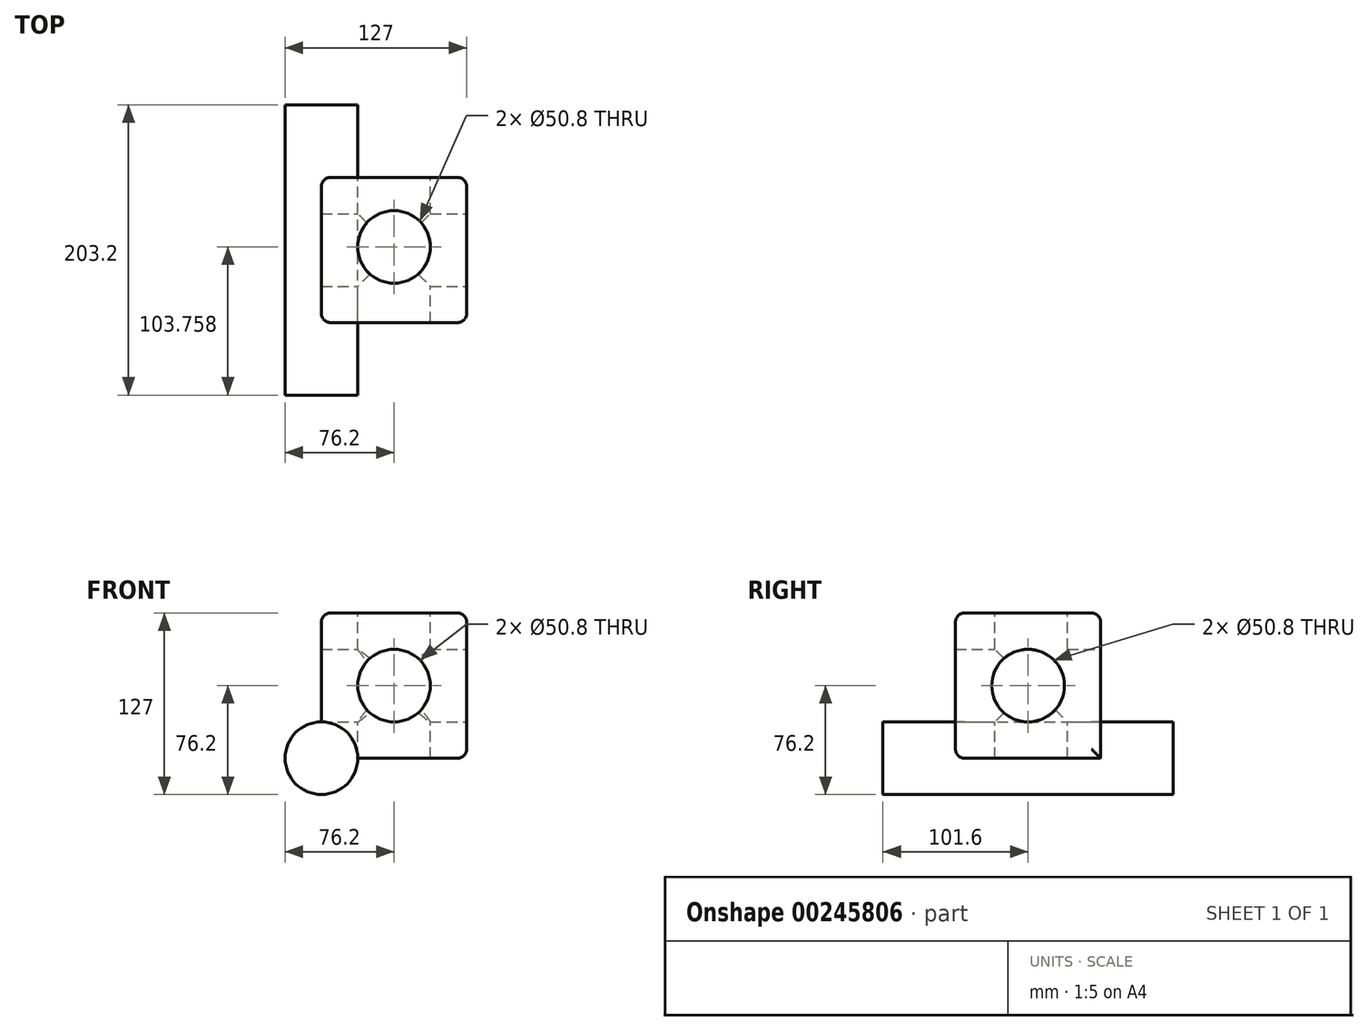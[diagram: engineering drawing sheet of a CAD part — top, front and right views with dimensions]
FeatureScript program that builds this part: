
annotation { "Feature Type Name" : "Feature", "Feature Type Description" : "" }
export const myFeature = defineFeature(function(context is Context, id is Id, definition is map)
    precondition{}
    {
        {
            var Q0;
            Q0=qCreatedBy(makeId("Front.planeOp"),FACE);
            var sketch = newSketch(context, id + "F0", { "sketchPlane" : qUnion([Q0])});
            skLineSegment(sketch, "E0", {"start": v(0, 0) * mm, "end": v(101.6, 0) * mm});
            skLineSegment(sketch, "E1", {"start": v(101.6, 0) * mm, "end": v(101.6, 101.6) * mm});
            skLineSegment(sketch, "E2", {"start": v(101.6, 101.6) * mm, "end": v(0, 101.6) * mm});
            skLineSegment(sketch, "E3", {"start": v(0, 101.6) * mm, "end": v(0, 0) * mm});
            skLineSegment(sketch, "E4", {"start": v(0, 3) * mm, "end": v(0, -3.73) * mm});
            skLineSegment(sketch, "E5", {"start": v(0, -3.73) * mm, "end": v(-10.09, -3.73) * mm});
            skSolve(sketch);
        }
        {
            var Q0;
            {var subQ1=sQuery(id+"F0.wireOp",EDGE,"E0");Q0=makeQuery(id+"F0.imprint","IMPRINT",FACE,{"disambiguationData":[TD([[makeQuery(id+"F0.imprint","IMPRINT",EDGE,{"derivedFrom":subQ1}),1.0]])]});}
            extrude(context, id + "F1", {"entities" : qUnion([Q0]), "depth" : 101.6 * mm});
        }
        {
            var Q0;
            Q0=makeQuery(id+"F1.opExtrude","SWEPT_FACE",FACE,{"disambiguationData":[OSD([sQuery(id+"F0.wireOp",EDGE,"E2")])]});
            var sketch = newSketch(context, id + "F2", { "sketchPlane" : qUnion([Q0])});
            skCircle(sketch, "E6", {"center": v(50.8, -48.64) * mm, "radius": 25.4 * mm});
            skPoint(sketch, "E7.orphan", {"position": v(50.8, 0) * mm});
            skPoint(sketch, "E8.end.orphan", {"position": v(50.8, -101.6) * mm});
            skSolve(sketch);
        }
        {
            var Q0;
            Q0=makeQuery(id+"F1.opExtrude","SWEPT_FACE",FACE,{"disambiguationData":[OSD([sQuery(id+"F0.wireOp",EDGE,"E1")])]});
            var sketch = newSketch(context, id + "F3", { "sketchPlane" : qUnion([Q0])});
            skCircle(sketch, "E9", {"center": v(-50.8, 50.8) * mm, "radius": 25.4 * mm});
            skPoint(sketch, "E10.orphan", {"position": v(-50.8, 101.6) * mm});
            skPoint(sketch, "E11.end.orphan", {"position": v(-50.8, 0) * mm});
            skSolve(sketch);
        }
        {
            var Q0;
            Q0=makeQuery(id+"F2.imprint","IMPRINT",FACE,{"disambiguationData":[TD([[makeQuery(id+"F2.imprint","IMPRINT",EDGE,{"derivedFrom":sQuery(id+"F2.wireOp",EDGE,"E6")}),1.0]])]});
            extrude(context, id + "F4", {"entities" : qUnion([Q0]), "operationType" : NewBodyOperationType.REMOVE, "oppositeDirection" : true, "depth" : 101.6 * mm});
        }
        {
            var Q0;
            Q0=makeQuery(id+"F3.imprint","IMPRINT",FACE,{"disambiguationData":[TD([[makeQuery(id+"F3.imprint","IMPRINT",EDGE,{"derivedFrom":sQuery(id+"F3.wireOp",EDGE,"E9")}),1.0]])]});
            extrude(context, id + "F5", {"entities" : qUnion([Q0]), "operationType" : NewBodyOperationType.REMOVE, "oppositeDirection" : true, "depth" : 101.6 * mm});
        }
        {
            var Q0;
            Q0=makeQuery(id+"F1.opExtrude","CAP_FACE",FACE,{"disambiguationData":[OSD([sQuery(id+"F0.wireOp",EDGE,"E0"),sQuery(id+"F0.wireOp",EDGE,"E1"),sQuery(id+"F0.wireOp",EDGE,"E2"),sQuery(id+"F0.wireOp",EDGE,"E3"),sQuery(id+"F0.wireOp",EDGE,"E4")])],"isStart":true});
            var sketch = newSketch(context, id + "F6", { "sketchPlane" : qUnion([Q0])});
            skCircle(sketch, "E12", {"center": v(-50.8, 50.8) * mm, "radius": 25.4 * mm});
            skPoint(sketch, "E13.orphan", {"position": v(-50.8, 101.6) * mm});
            skPoint(sketch, "E14.end.orphan", {"position": v(-50.8, 0) * mm});
            skSolve(sketch);
        }
        {
            var Q0;
            Q0=makeQuery(id+"F6.imprint","IMPRINT",FACE,{"disambiguationData":[TD([[makeQuery(id+"F6.imprint","IMPRINT",EDGE,{"derivedFrom":sQuery(id+"F6.wireOp",EDGE,"E12")}),1.0]])]});
            extrude(context, id + "F7", {"entities" : qUnion([Q0]), "operationType" : NewBodyOperationType.REMOVE, "oppositeDirection" : true, "depth" : 101.6 * mm});
        }
        {
            var Q0;
            Q0=makeQuery(id+"F1.opExtrude","SWEPT_EDGE",EDGE,{"disambiguationData":[OSD([sQuery(id+"F0.wireOp",EDGE,"E0"),sQuery(id+"F0.wireOp",EDGE,"E1")])]});
            var Q1;
            Q1=makeQuery(id+"F1.opExtrude","CAP_EDGE",EDGE,{"disambiguationData":[OSD([sQuery(id+"F0.wireOp",EDGE,"E1")])],"isStart":false});
            var Q2;
            Q2=makeQuery(id+"F1.opExtrude","CAP_EDGE",EDGE,{"disambiguationData":[OSD([sQuery(id+"F0.wireOp",EDGE,"E1")])],"isStart":true});
            var Q3;
            Q3=makeQuery(id+"F1.opExtrude","SWEPT_EDGE",EDGE,{"disambiguationData":[OSD([sQuery(id+"F0.wireOp",EDGE,"E1"),sQuery(id+"F0.wireOp",EDGE,"E2")])]});
            var Q4;
            Q4=makeQuery(id+"F1.opExtrude","CAP_EDGE",EDGE,{"disambiguationData":[OSD([sQuery(id+"F0.wireOp",EDGE,"E2")])],"isStart":false});
            var Q5;
            Q5=makeQuery(id+"F1.opExtrude","SWEPT_EDGE",EDGE,{"disambiguationData":[OSD([sQuery(id+"F0.wireOp",EDGE,"E2"),sQuery(id+"F0.wireOp",EDGE,"E3")])]});
            var Q6;
            Q6=makeQuery(id+"F1.opExtrude","CAP_EDGE",EDGE,{"disambiguationData":[OSD([sQuery(id+"F0.wireOp",EDGE,"E2")])],"isStart":true});
            var Q7;
            Q7=makeQuery(id+"F1.opExtrude","CAP_EDGE",EDGE,{"disambiguationData":[OSD([sQuery(id+"F0.wireOp",EDGE,"E0")])],"isStart":false});
            var Q8;
            Q8=makeQuery(id+"F1.opExtrude","CAP_EDGE",EDGE,{"disambiguationData":[OSD([sQuery(id+"F0.wireOp",EDGE,"E3"),sQuery(id+"F0.wireOp",EDGE,"E4")])],"isStart":false});
            var Q9;
            Q9=makeQuery(id+"F1.opExtrude","SWEPT_EDGE",EDGE,{"disambiguationData":[OSD([sQuery(id+"F0.wireOp",EDGE,"E0"),sQuery(id+"F0.wireOp",EDGE,"E4")])]});
            var Q10;
            Q10=makeQuery(id+"F1.opExtrude","CAP_EDGE",EDGE,{"disambiguationData":[OSD([sQuery(id+"F0.wireOp",EDGE,"E3"),sQuery(id+"F0.wireOp",EDGE,"E4")])],"isStart":true});
            fillet(context, id + "F8", {"entities" : qUnion([Q0, Q1, Q2, Q3, Q4, Q5, Q6, Q7, Q8, Q9, Q10]), "radius" : 6.35 * mm, "tangentPropagation" : true, "allowEdgeOverflow" : false});
        }
        {
            var Q0;
            Q0=qCreatedBy(makeId("Front.planeOp"),FACE);
            cPlane(context, id + "F9", {"entities" : qUnion([Q0]), "cplaneType" : CPlaneType.OFFSET, "offset" : 101.6 * mm, "width" : 152.4 * mm, "height" : 152.4 * mm});
        }
        {
            var Q0;
            Q0=qCreatedBy(id+"F9.planeOp",FACE);
            var sketch = newSketch(context, id + "F10", { "sketchPlane" : qUnion([Q0])});
            skCircle(sketch, "E15", {"center": v(0, 0) * mm, "radius": 25.4 * mm});
            skSolve(sketch);
        }
        {
            var Q0;
            Q0 = qSketchRegion(id + "F10", true);
            extrude(context, id + "F11", {"entities" : qUnion([Q0]), "operationType" : NewBodyOperationType.ADD, "depth" : 50.8 * mm, "hasSecondDirection" : true, "secondDirectionOppositeDirection" : true, "secondDirectionDepth" : 152.4 * mm});
        }
    });
